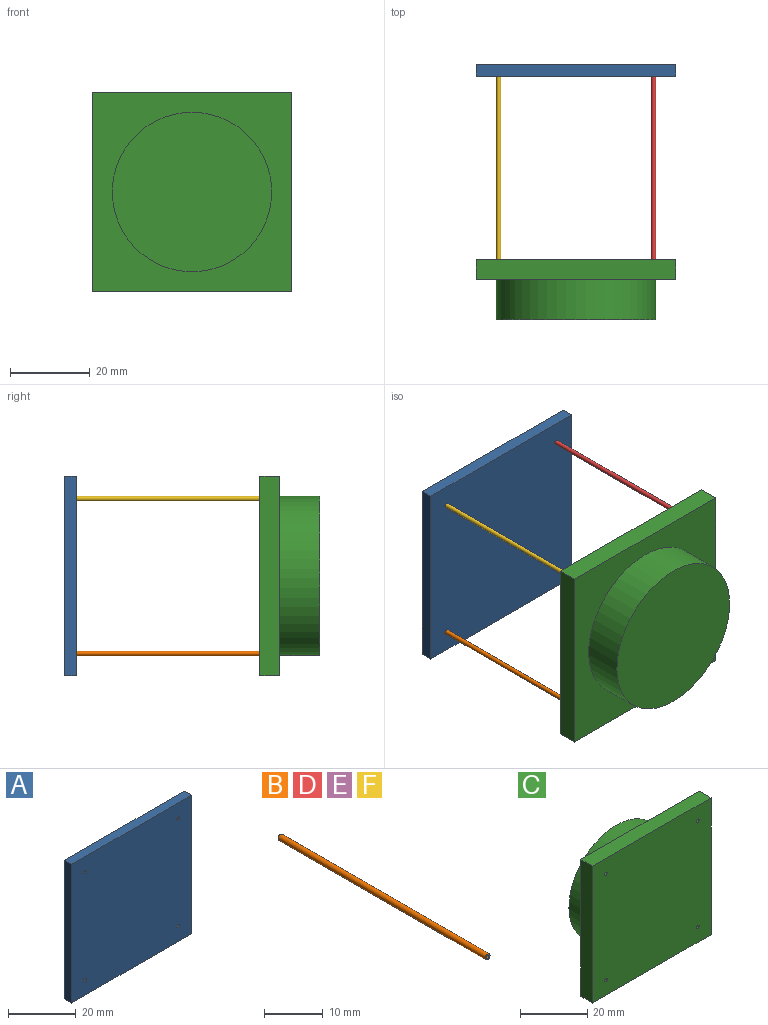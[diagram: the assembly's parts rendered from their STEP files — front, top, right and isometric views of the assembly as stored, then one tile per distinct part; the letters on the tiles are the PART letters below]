
ASSEMBLY  parts=6 mates=5
PART A: 14 faces, bbox 50x3x50 mm
  f0: plane 50x3mm, normal (0,0,1), area 150mm2, adj f1,f3,f4,f5
  f1: plane 50x3mm, normal (-1,0,0), area 150mm2, adj f0,f2,f4,f5
  f2: plane 50x3mm, normal (0,0,-1), area 150mm2, adj f1,f3,f4,f5
  f3: plane 50x3mm, normal (1,0,0), area 150mm2, adj f0,f2,f4,f5
  f4: plane 50x50mm, normal (0,1,0), area 2500mm2, adj f0,f1,f2,f3
  f5: plane 50x50mm, normal (0,-1,0), area 2495.9mm2, adj f0,f1,f2,f3,f6,f8,f10,f12
  f6: cylinder r=0.57mm len=2mm, axis (0,-1,0), area 7.2mm2, adj f5,f7
  f7: plane 1.14x1.14mm, normal (0,-1,0), area 1mm2, adj f6
  f8: cylinder r=0.57mm len=2mm, axis (0,-1,0), area 7.2mm2, adj f5,f9
  f9: plane 1.14x1.14mm, normal (0,-1,0), area 1mm2, adj f8
  f10: cylinder r=0.57mm len=2mm, axis (0,-1,0), area 7.2mm2, adj f5,f11
  f11: plane 1.14x1.14mm, normal (0,-1,0), area 1mm2, adj f10
  f12: cylinder r=0.57mm len=2mm, axis (0,-1,0), area 7.2mm2, adj f5,f13
  f13: plane 1.14x1.14mm, normal (0,-1,0), area 1mm2, adj f12
PART B: 4 faces, bbox 1.1x50x1.1 mm
  f0: cylinder r=0.31mm len=50mm, axis (0,1,0), area 97.4mm2, adj f2,f3
  f1: cylinder r=0.57mm len=50mm, axis (0,1,0), area 179.1mm2, adj f2,f3
  f2: plane 1.14x1.14mm, normal (0,-1,0), area 0.7mm2, adj f0,f1
  f3: plane 1.14x1.14mm, normal (0,1,0), area 0.7mm2, adj f0,f1
PART C: 16 faces, bbox 50x15x50 mm
  f0: plane 50x5mm, normal (0,0,1), area 250mm2, adj f1,f3,f4,f5
  f1: plane 50x5mm, normal (-1,0,0), area 250mm2, adj f0,f2,f4,f5
  f2: plane 50x5mm, normal (0,0,-1), area 250mm2, adj f1,f3,f4,f5
  f3: plane 50x5mm, normal (1,0,0), area 250mm2, adj f0,f2,f4,f5
  f4: plane 50x50mm, normal (0,1,0), area 1243.4mm2, adj f0,f1,f2,f3,f14
  f5: plane 50x50mm, normal (0,-1,0), area 2495.9mm2, adj f0,f1,f2,f3,f6,f8,f10,f12
  f6: cylinder r=0.57mm len=2mm, axis (0,-1,0), area 7.2mm2, adj f5,f7
  f7: plane 1.14x1.14mm, normal (0,-1,0), area 1mm2, adj f6
  f8: cylinder r=0.57mm len=2mm, axis (0,-1,0), area 7.2mm2, adj f5,f9
  f9: plane 1.14x1.14mm, normal (0,-1,0), area 1mm2, adj f8
  f10: cylinder r=0.57mm len=2mm, axis (0,-1,0), area 7.2mm2, adj f5,f11
  f11: plane 1.14x1.14mm, normal (0,-1,0), area 1mm2, adj f10
  f12: cylinder r=0.57mm len=2mm, axis (0,-1,0), area 7.2mm2, adj f5,f13
  f13: plane 1.14x1.14mm, normal (0,-1,0), area 1mm2, adj f12
  f14: cylinder r=20mm len=40mm, axis (0,-1,0), area 1256.6mm2, adj f4,f15
  f15: plane 40x40mm, normal (0,1,0), area 1256.6mm2, adj f14
PART D: same geometry as B
PART E: same geometry as B
PART F: same geometry as B
PLACE A t=(7.07,9.57,-34.35)mm
PLACE B t=(-12.36,11.57,-53.78)mm
PLACE C rot(axis=(0,0,1),180deg) t=(7.07,-36.43,-34.35)mm
PLACE D t=(26.5,11.57,-14.92)mm
PLACE E t=(26.5,11.57,-53.78)mm
PLACE F t=(-12.36,11.57,-14.92)mm
MATE fastened C.f6 <-> D.f1  axis (0,1,0) through (26.5,-38.43,-14.92)mm
MATE fastened A.f10 <-> B.f1  axis (0,-1,0) through (-12.36,11.57,-53.78)mm
MATE fastened C.f8 <-> B.f1  axis (0,1,0) through (-12.36,-38.43,-53.78)mm
MATE fastened C.f10 <-> E.f1  axis (0,1,0) through (26.5,-38.43,-53.78)mm
MATE fastened C.f12 <-> F.f1  axis (0,1,0) through (-12.36,-38.43,-14.92)mm
